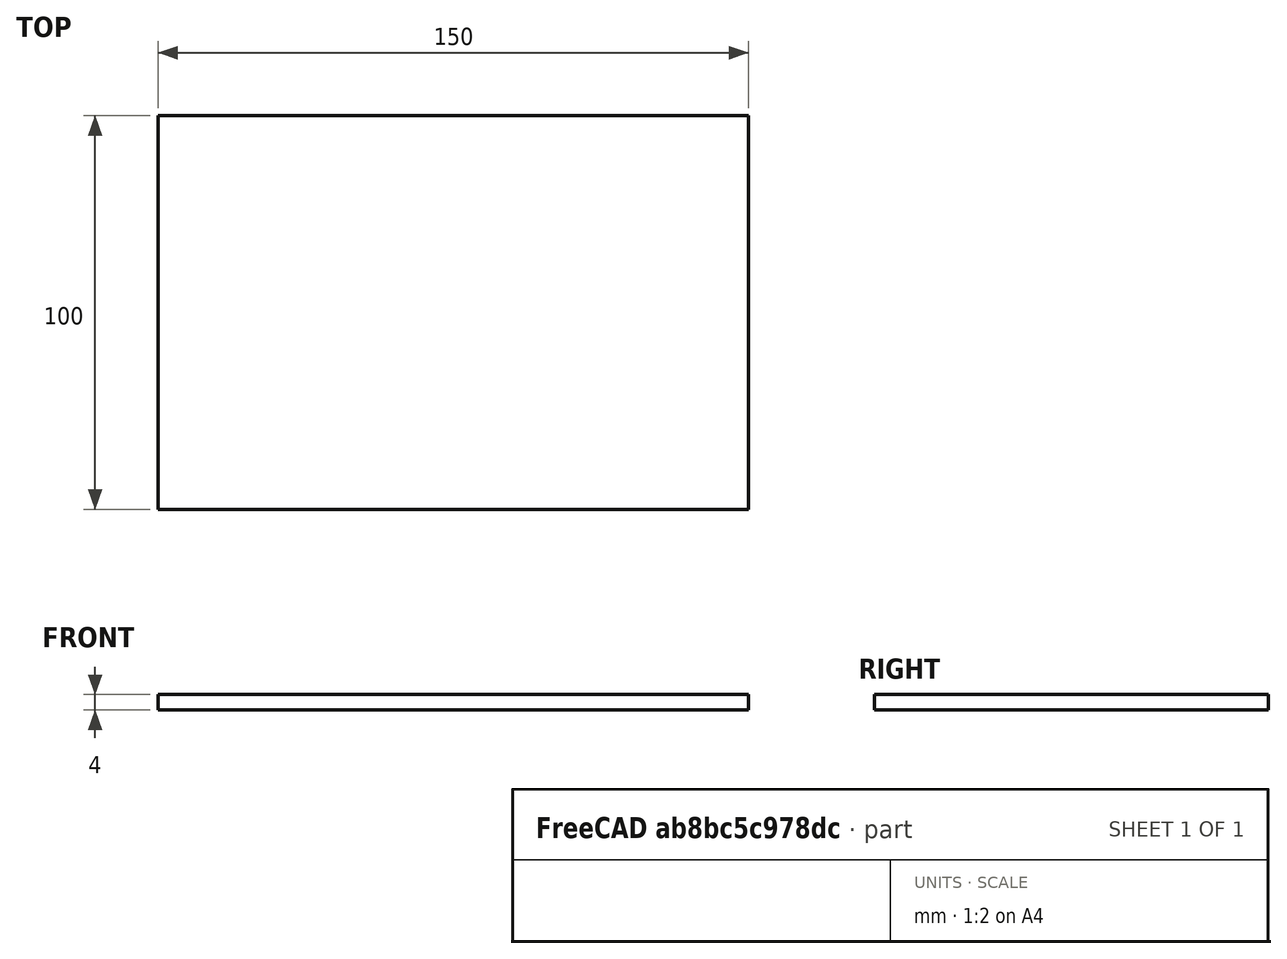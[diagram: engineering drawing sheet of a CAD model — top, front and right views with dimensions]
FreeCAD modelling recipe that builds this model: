
FCSTD DOCUMENT  (FreeCAD 0.17R13528 (Git))
Label: test
License: All rights reserved
LicenseURL: http://en.wikipedia.org/wiki/All_rights_reserved
objects: Sketcher::SketchObject×1, PartDesign::Pad×1, PartDesign::Body×1
note: 4 computed .brp shape members not serialized (recipe doc carries the construction recipe); baked Part::Feature solids carry a one-line shape summary decoded from their .brp

FEATURE [Sketcher::SketchObject] Sketch
  sketch-geometry (4):
    g0: LineSegment StartX=-150 StartY=0 StartZ=0 EndX=0 EndY=0 EndZ=0
    g1: LineSegment StartX=0 StartY=0 StartZ=0 EndX=0 EndY=-100 EndZ=0
    g2: LineSegment StartX=0 StartY=-100 StartZ=0 EndX=-150 EndY=-100 EndZ=0
    g3: LineSegment StartX=-150 StartY=-100 StartZ=0 EndX=-150 EndY=0 EndZ=0
  constraints (11):
    c: Coincident(g0,g1)
    c: Coincident(g1,g2)
    c: Coincident(g2,g3)
    c: Coincident(g3,g0)
    c: Horizontal(g0)
    c: Horizontal(g2)
    c: Vertical(g1)
    c: Vertical(g3)
    c: DistanceY(g3,g3) = 100
    c: DistanceX(g0,g0) = 150
    c: Coincident(g0,g-1)
FEATURE [PartDesign::Pad] Pad
  Length = 4
  Length2 = 100
  Profile = -> Sketch
  Type = 0
FEATURE [PartDesign::Body] Body
  Group = -> [Sketch,Pad]
  Origin = -> Origin
  Tip = -> Pad
